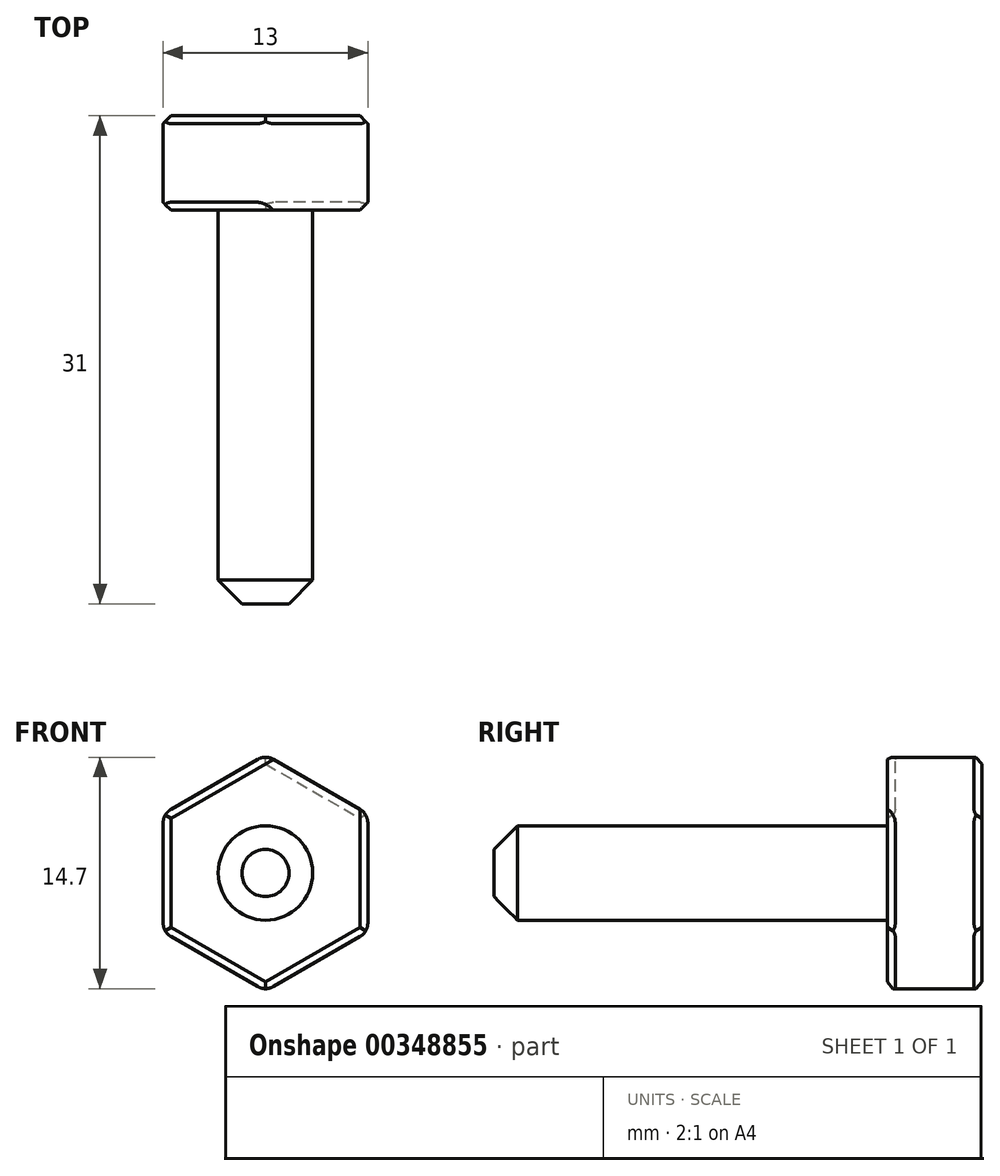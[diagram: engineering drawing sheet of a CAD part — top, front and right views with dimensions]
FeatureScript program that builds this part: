
annotation { "Feature Type Name" : "Feature", "Feature Type Description" : "" }
export const myFeature = defineFeature(function(context is Context, id is Id, definition is map)
    precondition{}
    {
        {
            var Q0;
            Q0=qCreatedBy(makeId("Front.planeOp"),FACE);
            var sketch = newSketch(context, id + "F0", { "sketchPlane" : qUnion([Q0])});
            skCircle(sketch, "E0.cCircle", {"center": v(0, 0) * mm, "radius": 6.5 * mm, "construction": true});
            skLineSegment(sketch, "E0.0", {"start": v(-6.5, 3.75) * mm, "end": v(0, 7.5) * mm});
            skLineSegment(sketch, "E0.1", {"start": v(0, 7.5) * mm, "end": v(6.5, 3.75) * mm});
            skLineSegment(sketch, "E0.2", {"start": v(6.5, 3.75) * mm, "end": v(6.5, -3.75) * mm});
            skLineSegment(sketch, "E0.3", {"start": v(6.5, -3.75) * mm, "end": v(0, -7.5) * mm});
            skLineSegment(sketch, "E0.4", {"start": v(0, -7.5) * mm, "end": v(-6.5, -3.75) * mm});
            skLineSegment(sketch, "E0.5", {"start": v(-6.5, -3.75) * mm, "end": v(-6.5, 3.75) * mm});
            skPoint(sketch, "E0.0.midPoint", {"position": v(-3.25, 5.63) * mm});
            skCircle(sketch, "E1", {"center": v(0, 0) * mm, "radius": 4 * mm});
            skSolve(sketch);
        }
        {
            var Q0;
            Q0=makeQuery(id+"F0.imprint","IMPRINT",FACE,{"disambiguationData":[TD([[makeQuery(id+"F0.imprint","IMPRINT",EDGE,{"derivedFrom":sQuery(id+"F0.wireOp",EDGE,"E1")}),1.0]])]});
            var Q1;
            Q1=makeQuery(id+"F0.imprint","IMPRINT",FACE,{"disambiguationData":[TD([[makeQuery(id+"F0.imprint","IMPRINT",EDGE,{"derivedFrom":sQuery(id+"F0.wireOp",EDGE,"E0.0")}),-1.0]])]});
            extrude(context, id + "F1", {"entities" : qUnion([Q0, Q1]), "oppositeDirection" : true, "depth" : 6 * mm});
        }
        {
            var Q0;
            Q0=makeQuery(id+"F1.opExtrude","CAP_FACE",FACE,{"disambiguationData":[OSD([sQuery(id+"F0.wireOp",EDGE,"E0.0"),sQuery(id+"F0.wireOp",EDGE,"E0.1"),sQuery(id+"F0.wireOp",EDGE,"E0.2"),sQuery(id+"F0.wireOp",EDGE,"E0.3"),sQuery(id+"F0.wireOp",EDGE,"E0.4"),sQuery(id+"F0.wireOp",EDGE,"E0.5")])],"isStart":true});
            var sketch = newSketch(context, id + "F2", { "sketchPlane" : qUnion([Q0])});
            skCircle(sketch, "E2", {"center": v(0, 0) * mm, "radius": 3 * mm});
            skSolve(sketch);
        }
        {
            var Q0;
            Q0=makeQuery(id+"F1.opExtrude","CAP_EDGE",EDGE,{"disambiguationData":[OSD([sQuery(id+"F0.wireOp",EDGE,"E0.2")])],"isStart":true});
            var Q1;
            Q1=makeQuery(id+"F1.opExtrude","CAP_EDGE",EDGE,{"disambiguationData":[OSD([sQuery(id+"F0.wireOp",EDGE,"E0.0")])],"isStart":true});
            var Q2;
            Q2=makeQuery(id+"F1.opExtrude","CAP_EDGE",EDGE,{"disambiguationData":[OSD([sQuery(id+"F0.wireOp",EDGE,"E0.5")])],"isStart":true});
            var Q3;
            Q3=makeQuery(id+"F1.opExtrude","CAP_EDGE",EDGE,{"disambiguationData":[OSD([sQuery(id+"F0.wireOp",EDGE,"E0.4")])],"isStart":true});
            var Q4;
            Q4=makeQuery(id+"F1.opExtrude","CAP_EDGE",EDGE,{"disambiguationData":[OSD([sQuery(id+"F0.wireOp",EDGE,"E0.3")])],"isStart":true});
            var Q5;
            Q5=makeQuery(id+"F1.opExtrude","CAP_FACE",FACE,{"disambiguationData":[OSD([sQuery(id+"F0.wireOp",EDGE,"E0.0"),sQuery(id+"F0.wireOp",EDGE,"E0.1"),sQuery(id+"F0.wireOp",EDGE,"E0.2"),sQuery(id+"F0.wireOp",EDGE,"E0.3"),sQuery(id+"F0.wireOp",EDGE,"E0.4"),sQuery(id+"F0.wireOp",EDGE,"E0.5")])],"isStart":false});
            chamfer(context, id + "F3", {"entities" : qUnion([Q0, Q1, Q2, Q3, Q4, Q5]), "width" : 0.5 * mm, "tangentPropagation" : true});
        }
        {
            var Q0;
            Q0=makeQuery(id+"F1.opExtrude","SWEPT_EDGE",EDGE,{"disambiguationData":[OSD([sQuery(id+"F0.wireOp",EDGE,"E0.0"),sQuery(id+"F0.wireOp",EDGE,"E0.1")])]});
            var Q1;
            Q1=makeQuery(id+"F1.opExtrude","SWEPT_EDGE",EDGE,{"disambiguationData":[OSD([sQuery(id+"F0.wireOp",EDGE,"E0.0"),sQuery(id+"F0.wireOp",EDGE,"E0.5")])]});
            var Q2;
            Q2=makeQuery(id+"F1.opExtrude","SWEPT_EDGE",EDGE,{"disambiguationData":[OSD([sQuery(id+"F0.wireOp",EDGE,"E0.1"),sQuery(id+"F0.wireOp",EDGE,"E0.2")])]});
            var Q3;
            Q3=makeQuery(id+"F1.opExtrude","SWEPT_EDGE",EDGE,{"disambiguationData":[OSD([sQuery(id+"F0.wireOp",EDGE,"E0.4"),sQuery(id+"F0.wireOp",EDGE,"E0.5")])]});
            var Q4;
            Q4=makeQuery(id+"F1.opExtrude","SWEPT_EDGE",EDGE,{"disambiguationData":[OSD([sQuery(id+"F0.wireOp",EDGE,"E0.3"),sQuery(id+"F0.wireOp",EDGE,"E0.4")])]});
            var Q5;
            Q5=makeQuery(id+"F1.opExtrude","SWEPT_EDGE",EDGE,{"disambiguationData":[OSD([sQuery(id+"F0.wireOp",EDGE,"E0.2"),sQuery(id+"F0.wireOp",EDGE,"E0.3")])]});
            fillet(context, id + "F4", {"entities" : qUnion([Q0, Q1, Q2, Q3, Q4, Q5]), "radius" : 1 * mm, "tangentPropagation" : true, "allowEdgeOverflow" : false});
        }
        {
            var Q0;
            Q0=makeQuery(id+"F2.imprint","IMPRINT",FACE,{"disambiguationData":[TD([[makeQuery(id+"F2.imprint","IMPRINT",EDGE,{"derivedFrom":sQuery(id+"F2.wireOp",EDGE,"E2")}),1.0]])]});
            extrude(context, id + "F5", {"entities" : qUnion([Q0]), "operationType" : NewBodyOperationType.ADD, "depth" : 25 * mm});
        }
        {
            var Q0;
            Q0=makeQuery(id+"F5.opExtrude","CAP_EDGE",EDGE,{"disambiguationData":[OSD([sQuery(id+"F2.wireOp",EDGE,"E2")])],"isStart":false});
            chamfer(context, id + "F6", {"entities" : qUnion([Q0]), "width" : 1.5 * mm, "tangentPropagation" : true});
        }
    });
